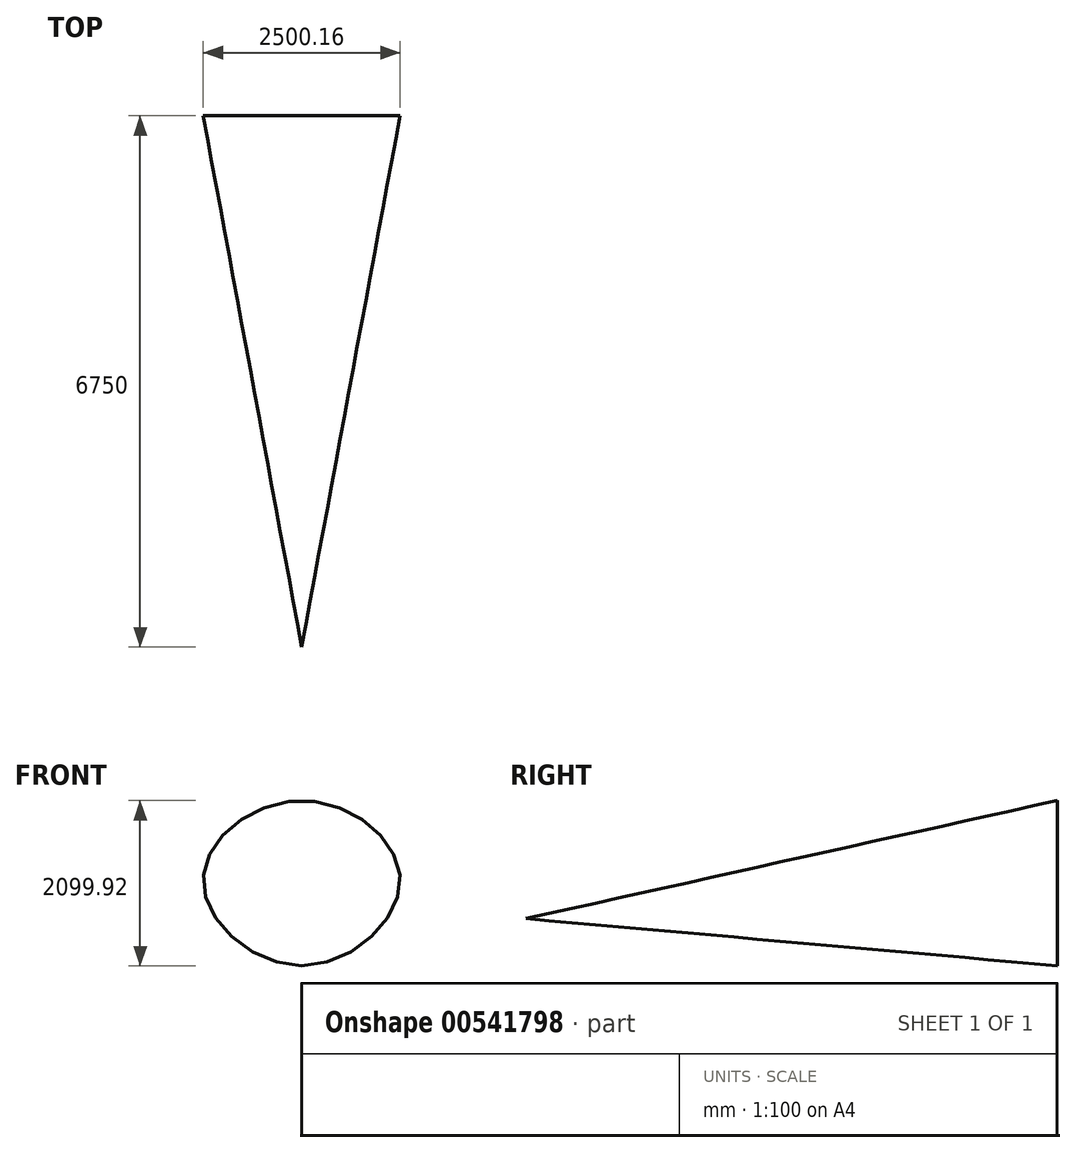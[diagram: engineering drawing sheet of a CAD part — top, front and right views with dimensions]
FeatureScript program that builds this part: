
annotation { "Feature Type Name" : "Feature", "Feature Type Description" : "" }
export const myFeature = defineFeature(function(context is Context, id is Id, definition is map)
    precondition{}
    {
        {
            var Q0;
            Q0=qCreatedBy(makeId("Front.planeOp"),FACE);
            cPlane(context, id + "F0", {"entities" : qUnion([Q0]), "cplaneType" : CPlaneType.OFFSET, "offset" : 8500 * mm, "width" : 150 * mm, "height" : 150 * mm});
        }
        {
            var Q0;
            Q0=qCreatedBy(makeId("Front.planeOp"),FACE);
            cPlane(context, id + "F1", {"entities" : qUnion([Q0]), "cplaneType" : CPlaneType.OFFSET, "offset" : 1750 * mm, "width" : 150 * mm, "height" : 150 * mm});
        }
        {
            var Q0;
            Q0=qCreatedBy(id+"F1.planeOp",FACE);
            var sketch = newSketch(context, id + "F2", { "sketchPlane" : qUnion([Q0])});
            skPoint(sketch, "E0.middle", {"position": v(0, 0) * mm});
            skFitSpline(sketch, "E1", {"points": [v(0, 1000) * mm, v(-1250, 0) * mm, v(0, -1099.92) * mm, v(1250, 0) * mm, v(0, 1000) * mm]});
            skSolve(sketch);
        }
        {
            var Q0;
            Q0=qCreatedBy(makeId("Right.planeOp"),FACE);
            var sketch = newSketch(context, id + "F3", { "sketchPlane" : qUnion([Q0])});
            skLineSegment(sketch, "E2", {"start": v(0, 0) * mm, "end": v(-8500, 0) * mm});
            skLineSegment(sketch, "E3", {"start": v(-8500, 0) * mm, "end": v(-8500, -500) * mm});
            skSolve(sketch);
        }
        {
            var Q0;
            Q0=sQuery(id+"F3.wireOp",VERTEX,"E3.end");
            var Q1;
            Q1=makeQuery(id+"F2.imprint","IMPRINT",FACE,{"disambiguationData":[TD([[makeQuery(id+"F2.imprint","IMPRINT",EDGE,{"derivedFrom":sQuery(id+"F2.wireOp",EDGE,"E1")}),1.0]])]});
            loft(context, id + "F4", {"sheetProfilesArray" : [{ "sheetProfileEntities" : qUnion([Q0]) }, { "sheetProfileEntities" : qUnion([Q1]) }]});
        }
    });
